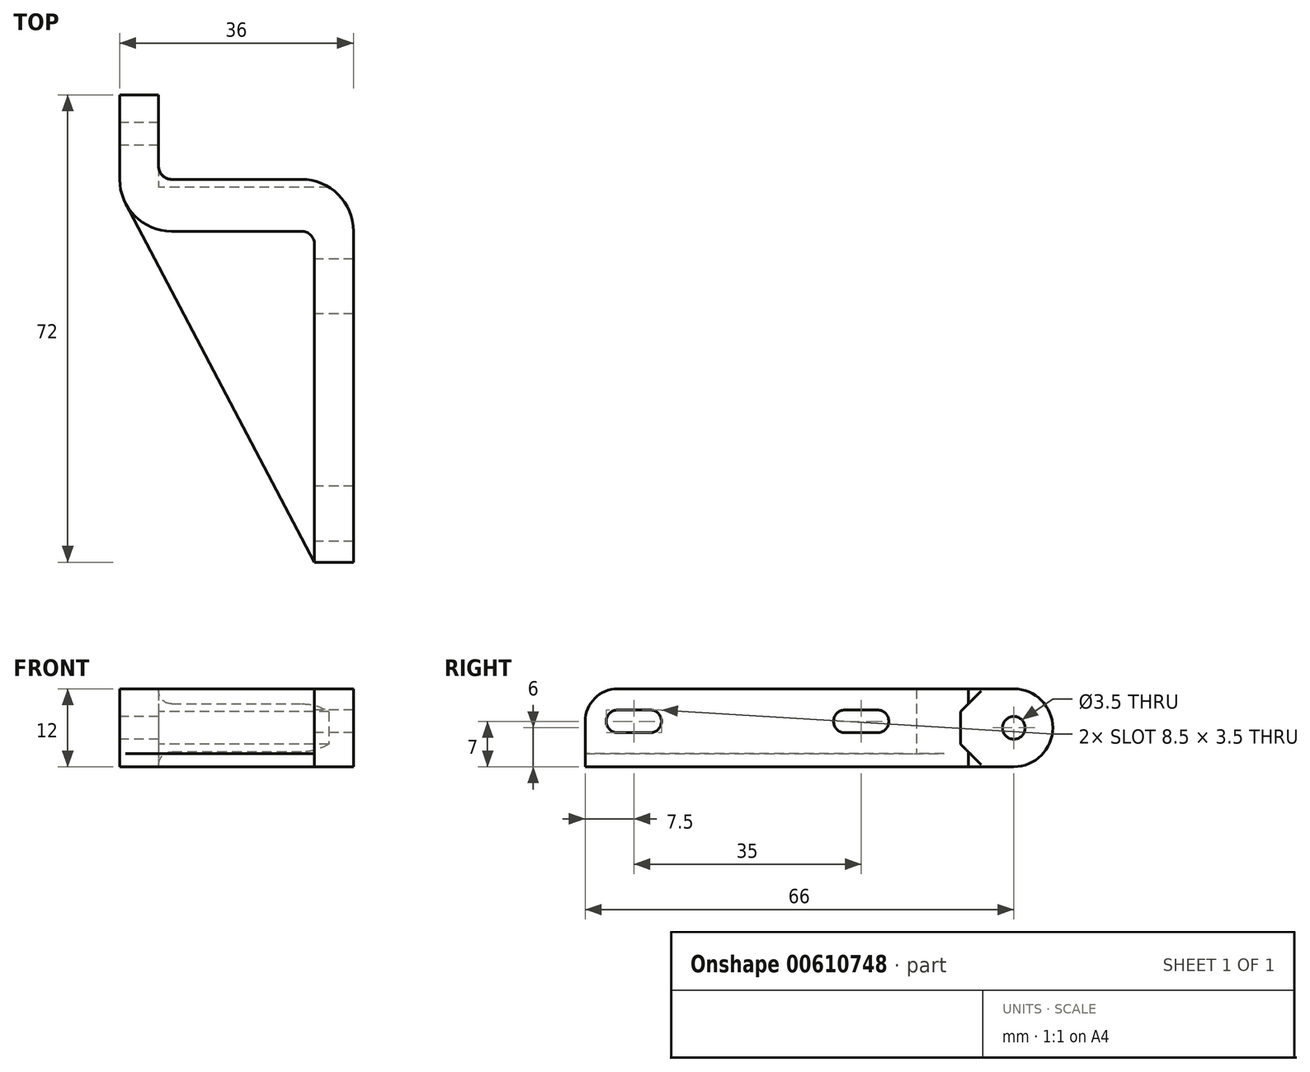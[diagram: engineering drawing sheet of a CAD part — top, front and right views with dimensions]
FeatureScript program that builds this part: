
annotation { "Feature Type Name" : "Feature", "Feature Type Description" : "" }
export const myFeature = defineFeature(function(context is Context, id is Id, definition is map)
    precondition{}
    {
        {
            var Q0;
            Q0=qCreatedBy(makeId("Top.planeOp"),FACE);
            var sketch = newSketch(context, id + "F0", { "sketchPlane" : qUnion([Q0])});
            skLineSegment(sketch, "E0", {"start": v(0, 0) * mm, "end": v(0, 51) * mm});
            skLineSegment(sketch, "E1", {"start": v(-8, 59) * mm, "end": v(-28, 59) * mm});
            skLineSegment(sketch, "E2", {"start": v(-30, 61) * mm, "end": v(-30, 72) * mm});
            skLineSegment(sketch, "E3", {"start": v(-30, 72) * mm, "end": v(-36, 72) * mm});
            skLineSegment(sketch, "E4", {"start": v(-36, 72) * mm, "end": v(-36, 59) * mm});
            skLineSegment(sketch, "E5", {"start": v(-28, 51) * mm, "end": v(-8, 51) * mm});
            skLineSegment(sketch, "E6", {"start": v(-6, 49) * mm, "end": v(-6, 0) * mm});
            skLineSegment(sketch, "E7", {"start": v(-6, 0) * mm, "end": v(0, 0) * mm});
            skPoint(sketch, "E8.visualSharp", {"position": v(-6, 51) * mm});
            skArc(sketch, "E8.filletArc", {"start": v(-6, 49) * mm, "mid": v(-6.59, 50.41) * mm, "end": v(-8, 51) * mm});
            skPoint(sketch, "E9.visualSharp", {"position": v(0, 59) * mm});
            skArc(sketch, "E9.filletArc", {"start": v(0, 51) * mm, "mid": v(-2.34, 56.66) * mm, "end": v(-8, 59) * mm});
            skPoint(sketch, "E10.visualSharp", {"position": v(-30, 59) * mm});
            skArc(sketch, "E10.filletArc", {"start": v(-30, 61) * mm, "mid": v(-29.41, 59.59) * mm, "end": v(-28, 59) * mm});
            skPoint(sketch, "E11.visualSharp", {"position": v(-36, 51) * mm});
            skArc(sketch, "E11.filletArc", {"start": v(-36, 59) * mm, "mid": v(-33.66, 53.34) * mm, "end": v(-28, 51) * mm});
            skLineSegment(sketch, "E12", {"start": v(-6, 0) * mm, "end": v(-35.08, 55.28) * mm});
            skSolve(sketch);
        }
        {
            var Q0;
            Q0=makeQuery(id+"F0.imprint","IMPRINT",FACE,{"disambiguationData":[TD([[makeQuery(id+"F0.imprint","IMPRINT",EDGE,{"derivedFrom":sQuery(id+"F0.wireOp",EDGE,"E0")}),1.0]])]});
            extrude(context, id + "F1", {"entities" : qUnion([Q0]), "depth" : 12 * mm, "offsetDistance" : 25 * mm});
        }
        {
            var Q0;
            {var subQ1=sQuery(id+"F0.wireOp",EDGE,"E5");Q0=makeQuery(id+"F0.imprint","IMPRINT",FACE,{"disambiguationData":[TD([[makeQuery(id+"F0.imprint","IMPRINT",EDGE,{"derivedFrom":subQ1}),-1.0]])]});}
            extrude(context, id + "F2", {"entities" : qUnion([Q0]), "operationType" : NewBodyOperationType.ADD, "depth" : 2 * mm, "offsetDistance" : 25 * mm});
        }
        {
            var Q0;
            Q0=makeQuery(id+"F1.opExtrude","SWEPT_FACE",FACE,{"disambiguationData":[OSD([sQuery(id+"F0.wireOp",EDGE,"E6")])]});
            var sketch = newSketch(context, id + "F3", { "sketchPlane" : qUnion([Q0])});
            skLineSegment(sketch, "E13", {"start": v(7, 0) * mm, "end": v(7, 55) * mm});
            skLineSegment(sketch, "E14", {"start": v(-7, 55) * mm, "end": v(-7, 0) * mm});
            skCircle(sketch, "E15", {"center": v(0, 0) * mm, "radius": 2 * mm, "construction": true});
            skCircle(sketch, "E16", {"center": v(0, 35) * mm, "radius": 2 * mm, "construction": true});
            skCircle(sketch, "E17", {"center": v(0, 0) * mm, "radius": 7 * mm, "construction": true});
            skArc(sketch, "E18", {"start": v(-7, 0) * mm, "mid": v(0, -7) * mm, "end": v(7, 0) * mm});
            skLineSegment(sketch, "E19", {"start": v(0, 53) * mm, "end": v(0, 0) * mm, "construction": true});
            skLineSegment(sketch, "E20", {"start": v(-2, 0) * mm, "end": v(-2, 10) * mm});
            skArc(sketch, "E21", {"start": v(2, 10) * mm, "mid": v(0, 12) * mm, "end": v(-2, 10) * mm});
            skLineSegment(sketch, "E22", {"start": v(2, 10) * mm, "end": v(2, 0) * mm});
            skArc(sketch, "E23", {"start": v(-2, 0) * mm, "mid": v(0, -2) * mm, "end": v(2, 0) * mm});
            skLineSegment(sketch, "E24", {"start": v(-2, 35) * mm, "end": v(-2, 45) * mm});
            skArc(sketch, "E25", {"start": v(2, 45) * mm, "mid": v(0, 47) * mm, "end": v(-2, 45) * mm});
            skLineSegment(sketch, "E26", {"start": v(2, 45) * mm, "end": v(2, 35) * mm});
            skArc(sketch, "E27", {"start": v(-2, 35) * mm, "mid": v(0, 33) * mm, "end": v(2, 35) * mm});
            skCircle(sketch, "E28", {"center": v(0, 45) * mm, "radius": 4 * mm, "construction": true});
            skLineSegment(sketch, "E29", {"start": v(-7, 55) * mm, "end": v(7, 55) * mm});
            skLineSegment(sketch, "E30", {"start": v(7, 49) * mm, "end": v(-7, 49) * mm, "construction": true});
            skSolve(sketch);
        }
        {
            var Q0;
            {var subQ1=sQuery(id+"F0.wireOp",EDGE,"E6");var subQ6=makeQuery(id+"F1.opExtrude","SWEPT_EDGE",EDGE,{"disambiguationData":[OSD([subQ1,sQuery(id+"F0.wireOp",EDGE,"E8.filletArc")])]});Q0=makeQuery(id+"F3.imprint","IMPRINT",FACE,{"disambiguationData":[TD([[makeQuery(id+"F3.imprint","IMPRINT",EDGE,{"derivedFrom":subQ6}),1.0]])]});}
            var sketch = newSketch(context, id + "F4", { "sketchPlane" : qUnion([Q0])});
            skArc(sketch, "E31", {"start": v(0, 7) * mm, "mid": v(-1.46, 10.54) * mm, "end": v(-5, 12) * mm});
            skLineSegment(sketch, "E32", {"start": v(0, 12) * mm, "end": v(-5, 12) * mm});
            skCircle(sketch, "E33", {"center": v(-5, 7) * mm, "radius": 1.75 * mm, "construction": true});
            skLineSegment(sketch, "E34", {"start": v(-5, 8.75) * mm, "end": v(-10, 8.75) * mm});
            skArc(sketch, "E35", {"start": v(-10, 8.75) * mm, "mid": v(-11.75, 7) * mm, "end": v(-10, 5.25) * mm});
            skLineSegment(sketch, "E36", {"start": v(-5, 5.25) * mm, "end": v(-10, 5.25) * mm});
            skArc(sketch, "E37", {"start": v(-5, 5.25) * mm, "mid": v(-3.25, 7) * mm, "end": v(-5, 8.75) * mm});
            skCircle(sketch, "E38", {"center": v(-40, 7) * mm, "radius": 1.75 * mm, "construction": true});
            skLineSegment(sketch, "E39", {"start": v(-40, 8.75) * mm, "end": v(-45, 8.75) * mm});
            skArc(sketch, "E40", {"start": v(-45, 8.75) * mm, "mid": v(-46.75, 7) * mm, "end": v(-45, 5.25) * mm});
            skLineSegment(sketch, "E41", {"start": v(-40, 5.25) * mm, "end": v(-45, 5.25) * mm});
            skArc(sketch, "E42", {"start": v(-40, 5.25) * mm, "mid": v(-38.25, 7) * mm, "end": v(-40, 8.75) * mm});
            skPoint(sketch, "E43.orphan", {"position": v(-6, 0) * mm});
            skLineSegment(sketch, "E44", {"start": v(0, 12) * mm, "end": v(0, 7) * mm});
            skSolve(sketch);
        }
        {
            var Q0;
            Q0 = qSketchRegion(id + "F4", true);
            extrude(context, id + "F5", {"entities" : qUnion([Q0]), "operationType" : NewBodyOperationType.REMOVE, "endBound" : BoundingType.UP_TO_NEXT, "oppositeDirection" : true, "depth" : 25 * mm, "offsetDistance" : 25 * mm});
        }
        {
            var Q0;
            Q0=makeQuery(id+"F1.opExtrude","SWEPT_FACE",FACE,{"disambiguationData":[OSD([sQuery(id+"F0.wireOp",EDGE,"E4")])]});
            var sketch = newSketch(context, id + "F6", { "sketchPlane" : qUnion([Q0])});
            skArc(sketch, "E45", {"start": v(-66, 12) * mm, "mid": v(-72, 6) * mm, "end": v(-66, 0) * mm});
            skCircle(sketch, "E46", {"center": v(-66, 6) * mm, "radius": 1.75 * mm});
            skSolve(sketch);
        }
        {
            var Q0;
            Q0 = qSketchRegion(id + "F6", true);
            var Q1;
            {var subQ0=sQuery(id+"F6.wireOp",EDGE,"E45");var subQ1=sQuery(id+"F0.wireOp",EDGE,"E4");var subQ2=makeQuery(id+"F1.opExtrude","CAP_EDGE",EDGE,{"disambiguationData":[OSD([subQ1])],"isStart":false});var subQ3=makeQuery(id+"F6.imprint","INTERSECT",VERTEX,{"derivedFrom":[subQ2,subQ0]});Q1=makeQuery(id+"F6.imprint","IMPRINT",FACE,{"disambiguationData":[TD([[makeQuery(id+"F6.imprint","IMPRINT",EDGE,{"disambiguationData":[TD([[subQ3,-1.0]])],"derivedFrom":subQ0}),-1.0]])]});}
            var Q2;
            {var subQ0=sQuery(id+"F6.wireOp",EDGE,"E45");var subQ1=sQuery(id+"F0.wireOp",EDGE,"E4");var subQ2=makeQuery(id+"F1.opExtrude","CAP_EDGE",EDGE,{"disambiguationData":[OSD([subQ1])],"isStart":true});var subQ3=makeQuery(id+"F6.imprint","INTERSECT",VERTEX,{"derivedFrom":[subQ2,subQ0]});Q2=makeQuery(id+"F6.imprint","IMPRINT",FACE,{"disambiguationData":[TD([[makeQuery(id+"F6.imprint","IMPRINT",EDGE,{"disambiguationData":[TD([[subQ3,1.0]])],"derivedFrom":subQ0}),-1.0]])]});}
            extrude(context, id + "F7", {"entities" : qUnion([Q0, Q1, Q2]), "operationType" : NewBodyOperationType.REMOVE, "endBound" : BoundingType.UP_TO_NEXT, "oppositeDirection" : true, "depth" : 25 * mm, "offsetDistance" : 25 * mm});
        }
        {
            var Q0;
            Q0=makeQuery(id+"F1.opExtrude","SWEPT_FACE",FACE,{"disambiguationData":[OSD([sQuery(id+"F0.wireOp",EDGE,"E2")])]});
            var sketch = newSketch(context, id + "F8", { "sketchPlane" : qUnion([Q0])});
            skLineSegment(sketch, "E47", {"start": v(66, 6) * mm, "end": v(57.8, 6) * mm, "construction": true});
            skLineSegment(sketch, "E48", {"start": v(57.8, 8.5) * mm, "end": v(57.8, 3.5) * mm});
            skLineSegment(sketch, "E49", {"start": v(57.8, 3.5) * mm, "end": v(66, -4.7) * mm});
            skLineSegment(sketch, "E50", {"start": v(66, -4.7) * mm, "end": v(66, 16.7) * mm});
            skLineSegment(sketch, "E51", {"start": v(66, 16.7) * mm, "end": v(57.8, 8.5) * mm});
            skSolve(sketch);
        }
        {
            var Q0;
            Q0 = qSketchRegion(id + "F8", true);
            extrude(context, id + "F9", {"entities" : qUnion([Q0]), "operationType" : NewBodyOperationType.REMOVE, "endBound" : BoundingType.THROUGH_ALL, "depth" : 25 * mm, "offsetDistance" : 25 * mm});
        }
    });
